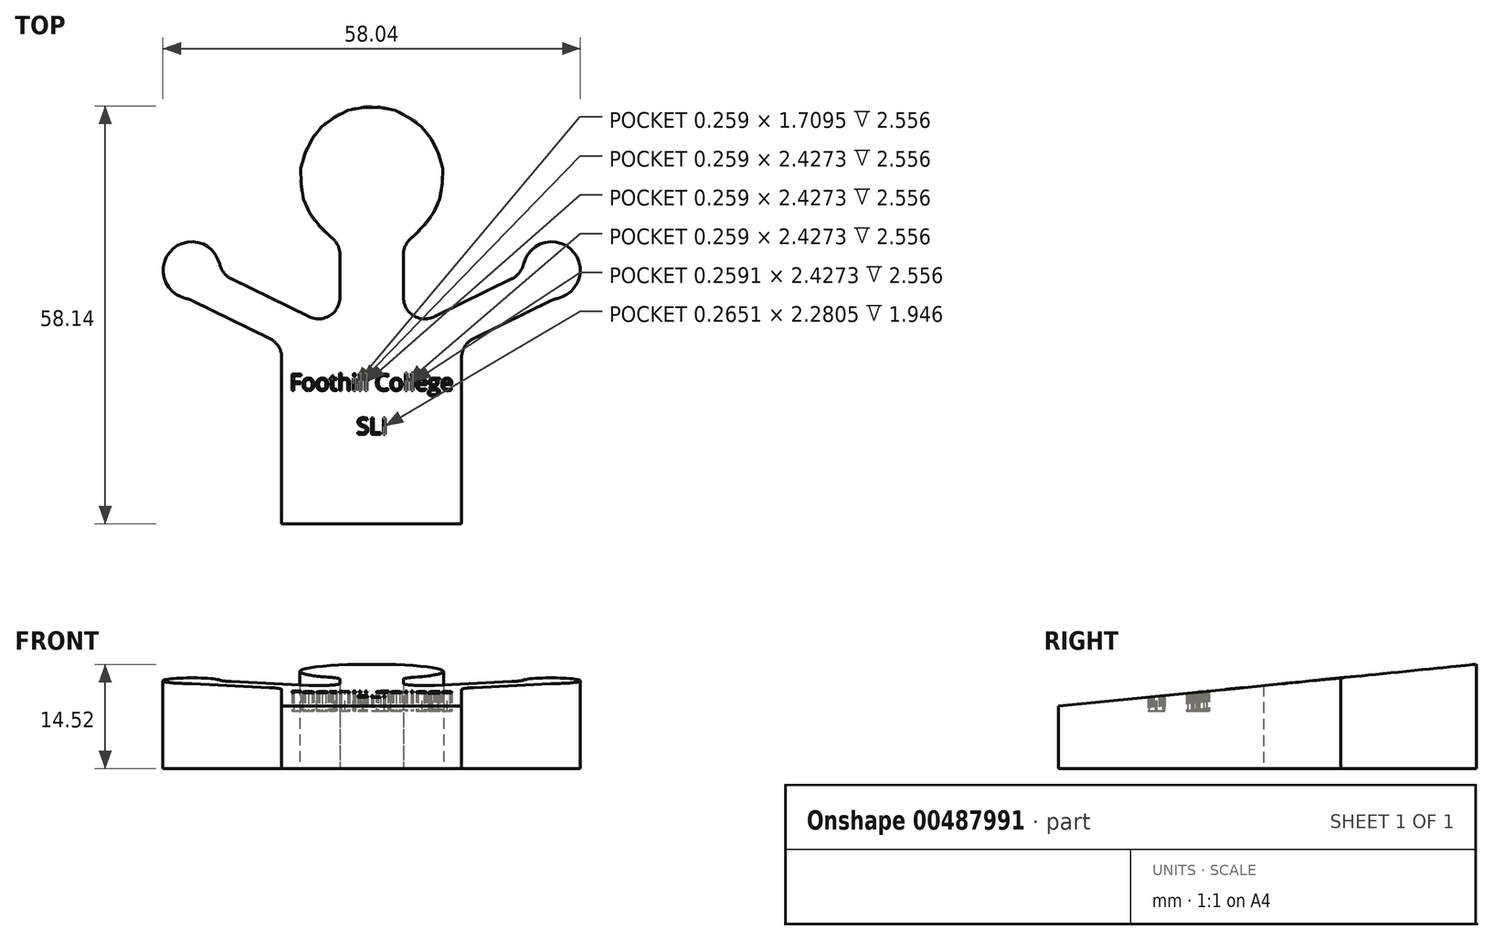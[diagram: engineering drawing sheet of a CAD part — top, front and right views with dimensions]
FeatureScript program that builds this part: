
annotation { "Feature Type Name" : "Feature", "Feature Type Description" : "" }
export const myFeature = defineFeature(function(context is Context, id is Id, definition is map)
    precondition{}
    {
        {
            var Q0;
            Q0=qCreatedBy(makeId("Right.planeOp"),FACE);
            var sketch = newSketch(context, id + "F0", { "sketchPlane" : qUnion([Q0])});
            skLineSegment(sketch, "E0", {"start": v(-18.87, 8.7) * mm, "end": v(41.85, 14.78) * mm});
            skSolve(sketch);
        }
        {
            var Q0;
            Q0=sQuery(id+"F0.wireOp",EDGE,"E0");
            cPlane(context, id + "F1", {"entities" : qUnion([Q0]), "cplaneType" : CPlaneType.LINE_ANGLE, "offset" : 25 * mm, "angle" : 0 * degree, "width" : 150 * mm, "height" : 150 * mm});
        }
        {
            var Q0;
            Q0=qCreatedBy(makeId("Top.planeOp"),FACE);
            var sketch = newSketch(context, id + "F2", { "sketchPlane" : qUnion([Q0])});
            skArc(sketch, "E1", {"start": v(0, 39.27) * mm, "mid": v(-9.54, 32.25) * mm, "end": v(-5.7, 21.05) * mm});
            skLineSegment(sketch, "E2.top", {"start": v(-12.5, -18.87) * mm, "end": v(0, -18.87) * mm});
            skLineSegment(sketch, "E2.left", {"start": v(-12.5, 4.26) * mm, "end": v(-12.5, -18.87) * mm});
            skLineSegment(sketch, "E3", {"start": v(-14.18, 6.95) * mm, "end": v(-24.96, 12.23) * mm});
            skArc(sketch, "E4", {"start": v(-21.12, 17.28) * mm, "mid": v(-27.9, 19.2) * mm, "end": v(-25.74, 12.48) * mm});
            skLineSegment(sketch, "E5", {"start": v(-4.4, 18.59) * mm, "end": v(-4.4, 12.66) * mm});
            skLineSegment(sketch, "E6", {"start": v(-19.5, 15.23) * mm, "end": v(-8.72, 9.96) * mm});
            skArc(sketch, "E7.filletArc", {"start": v(-21.12, 17.28) * mm, "mid": v(-20.54, 16.07) * mm, "end": v(-19.5, 15.23) * mm});
            skArc(sketch, "E8.filletArc", {"start": v(-24.96, 12.23) * mm, "mid": v(-25.34, 12.38) * mm, "end": v(-25.74, 12.48) * mm});
            skPoint(sketch, "E9.visualSharp", {"position": v(-4.4, 7.85) * mm});
            skArc(sketch, "E9.filletArc", {"start": v(-8.72, 9.96) * mm, "mid": v(-5.82, 10.11) * mm, "end": v(-4.4, 12.66) * mm});
            skPoint(sketch, "E10.visualSharp", {"position": v(-12.5, 6.13) * mm});
            skArc(sketch, "E10.filletArc", {"start": v(-12.5, 4.26) * mm, "mid": v(-12.96, 5.85) * mm, "end": v(-14.18, 6.95) * mm});
            skPoint(sketch, "E11.visualSharp", {"position": v(-4.4, 20.3) * mm});
            skArc(sketch, "E11.filletArc", {"start": v(-4.4, 18.59) * mm, "mid": v(-4.75, 19.98) * mm, "end": v(-5.7, 21.05) * mm});
            skArc(sketch, "E12.MirrorCS", {"start": v(4.4, 18.59) * mm, "mid": v(4.75, 19.98) * mm, "end": v(5.7, 21.05) * mm});
            skArc(sketch, "E13.MirrorCS", {"start": v(24.96, 12.23) * mm, "mid": v(25.34, 12.38) * mm, "end": v(25.74, 12.48) * mm});
            skArc(sketch, "E14.MirrorCS", {"start": v(21.12, 17.28) * mm, "mid": v(20.54, 16.07) * mm, "end": v(19.5, 15.23) * mm});
            skArc(sketch, "E15.MirrorCS", {"start": v(12.5, 4.26) * mm, "mid": v(12.96, 5.85) * mm, "end": v(14.18, 6.95) * mm});
            skArc(sketch, "E16.MirrorCS", {"start": v(0, 39.27) * mm, "mid": v(9.54, 32.25) * mm, "end": v(5.7, 21.05) * mm});
            skLineSegment(sketch, "E17.MirrorCS", {"start": v(12.5, -18.87) * mm, "end": v(0, -18.87) * mm});
            skPoint(sketch, "E18.MirrorP", {"position": v(4.4, 7.85) * mm});
            skArc(sketch, "E19.MirrorCS", {"start": v(21.12, 17.28) * mm, "mid": v(27.9, 19.2) * mm, "end": v(25.74, 12.48) * mm});
            skLineSegment(sketch, "E20.MirrorCS", {"start": v(19.5, 15.23) * mm, "end": v(8.72, 9.96) * mm});
            skLineSegment(sketch, "E21.MirrorCS", {"start": v(14.18, 6.95) * mm, "end": v(24.96, 12.23) * mm});
            skArc(sketch, "E22.MirrorCS", {"start": v(8.72, 9.96) * mm, "mid": v(5.82, 10.11) * mm, "end": v(4.4, 12.66) * mm});
            skPoint(sketch, "E23.MirrorP", {"position": v(4.4, 20.3) * mm});
            skPoint(sketch, "E24.MirrorP", {"position": v(12.5, 6.13) * mm});
            skLineSegment(sketch, "E25.MirrorCS", {"start": v(4.4, 18.59) * mm, "end": v(4.4, 12.66) * mm});
            skLineSegment(sketch, "E26.MirrorCS", {"start": v(12.5, 4.26) * mm, "end": v(12.5, -18.87) * mm});
            skSolve(sketch);
        }
        {
            var Q0;
            Q0 = qSketchRegion(id + "F2", true);
            var Q1;
            Q1=qCreatedBy(id+"F1.planeOp",FACE);
            extrude(context, id + "F3", {"entities" : qUnion([Q0]), "endBound" : BoundingType.UP_TO_SURFACE, "endBoundEntityFace" : qUnion([Q1]), "depth" : 25 * mm});
        }
        {
            var Q0;
            Q0=qCreatedBy(makeId("Top.planeOp"),FACE);
            cPlane(context, id + "F4", {"entities" : qUnion([Q0]), "cplaneType" : CPlaneType.OFFSET, "offset" : 8 * mm, "width" : 150 * mm, "height" : 150 * mm});
        }
        {
            var Q0;
            Q0=qCreatedBy(id+"F4.planeOp",FACE);
            var sketch = newSketch(context, id + "F5", { "sketchPlane" : qUnion([Q0])});
            skText(sketch, "E27", { "text": "Foothill College", "fontName": "OpenSans-Regular.ttf"});
            skText(sketch, "E28", { "text": "SLI", "fontName": "OpenSans-Regular.ttf"});
            const initialGuessF5  = {"E27": [-0.0114, -0.0003, 1, 0, 0.0023], "E28": [-0.0021, -0.00638, 1, 0, 0.0023]};
            skSetInitialGuess(sketch, initialGuessF5);
            skSolve(sketch);
        }
        {
            var Q0;
            Q0 = qSketchRegion(id + "F5", true);
            extrude(context, id + "F6", {"entities" : qUnion([Q0]), "operationType" : NewBodyOperationType.REMOVE, "depth" : 25 * mm, "offsetDistance" : 25 * mm});
        }
    });
